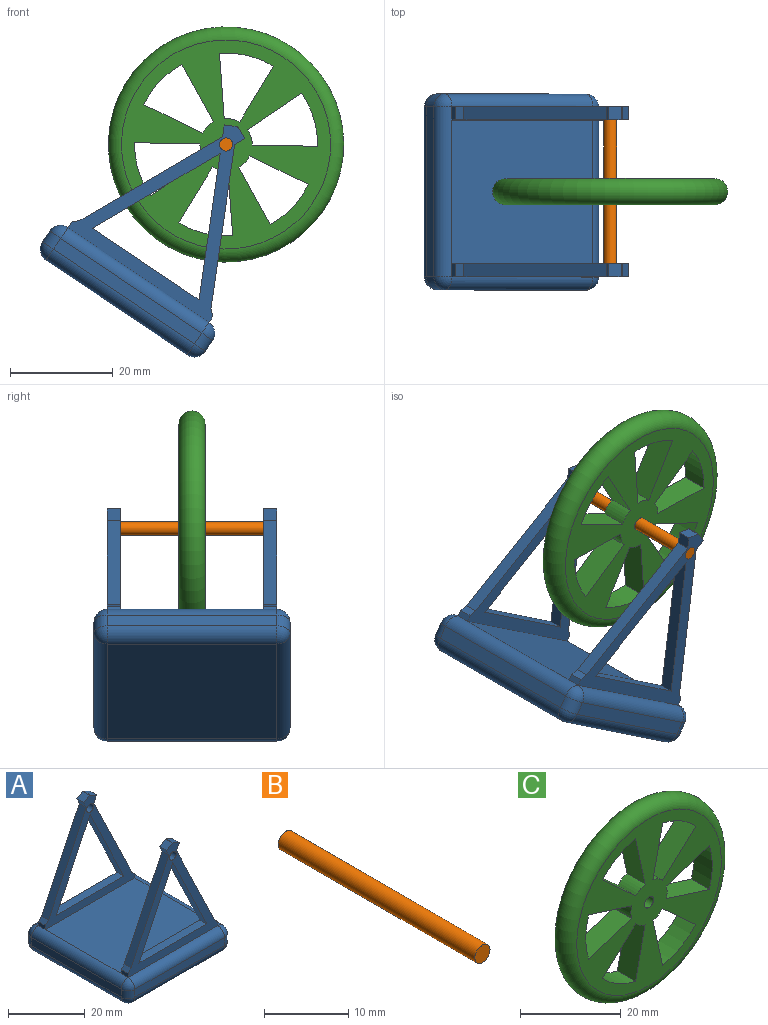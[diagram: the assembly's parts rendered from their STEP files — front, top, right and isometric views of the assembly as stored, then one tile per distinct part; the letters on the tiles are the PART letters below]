
ASSEMBLY  parts=3 mates=2
PART A: 60 faces, bbox 38.1x38.1x42.2 mm
  f0: plane 24.94x2.54mm, normal (0,0,1), area 63.3mm2, adj f1,f32,f34,f50
  f1: plane 25.94x12.47mm, normal (0.9,0,-0.43), area 73.1mm2, adj f0,f32,f34,f50
  f2: plane 28.96x13.92mm, normal (-0.9,0,0.43), area 81.6mm2, adj f32,f34,f49,f53
  f3: plane 24.94x2.54mm, normal (0,0,1), area 63.3mm2, adj f4,f37,f39,f46
  f4: plane 25.94x12.47mm, normal (0.9,0,-0.43), area 73.1mm2, adj f3,f37,f39,f46
  f5: plane 28.96x13.92mm, normal (-0.9,0,0.43), area 81.6mm2, adj f37,f39,f45,f52
  f6: plane 33.02x27.94mm, normal (0,0,1), area 922.6mm2, adj f16,f25,f32,f37
  f7: plane 33.02x2.54mm, normal (-1,0,0), area 83.9mm2, adj f20,f25,f28,f31
  f8: plane 33.02x2.54mm, normal (0,-1,0), area 83.9mm2, adj f17,f26,f27,f31
  f9: plane 33.02x2.54mm, normal (1,0,0), area 83.9mm2, adj f12,f16,f17,f18
  f10: plane 33.02x2.54mm, normal (0,1,0), area 83.9mm2, adj f12,f15,f19,f20
  f11: plane 33.02x33.02mm, normal (0,0,-1), area 1090.3mm2, adj f18,f19,f27,f28
  f12: cylinder r=2.54mm len=2.54mm, axis (0,0,1), area 10.1mm2, adj f9,f10,f13,f14
  f13: sphere r=2.54mm, area 10.1mm2, adj f12,f15,f16
  f14: sphere r=2.54mm, area 10.1mm2, adj f12,f18,f19
  f15: cylinder r=2.54mm len=33.02mm, axis (1,0,0), area 131.7mm2, adj f10,f13,f21,f34
  f16: cylinder r=2.54mm len=33.02mm, axis (0,-1,0), area 131.7mm2, adj f6,f9,f13,f22,f33,f36
  f17: cylinder r=2.54mm len=2.54mm, axis (0,0,-1), area 10.1mm2, adj f8,f9,f22,f23
  f18: cylinder r=2.54mm len=33.02mm, axis (0,1,0), area 131.7mm2, adj f9,f11,f14,f23
  f19: cylinder r=2.54mm len=33.02mm, axis (-1,0,0), area 131.7mm2, adj f10,f11,f14,f24
  f20: cylinder r=2.54mm len=2.54mm, axis (0,0,-1), area 10.1mm2, adj f7,f10,f21,f24
  f21: sphere r=2.54mm, area 10.1mm2, adj f15,f20,f25
  f22: sphere r=2.54mm, area 10.1mm2, adj f16,f17,f26
  f23: sphere r=2.54mm, area 10.1mm2, adj f17,f18,f27
  f24: sphere r=2.54mm, area 10.1mm2, adj f19,f20,f28
  f25: cylinder r=2.54mm len=33.02mm, axis (0,1,0), area 131.7mm2, adj f6,f7,f21,f29,f35,f38
  f26: cylinder r=2.54mm len=33.02mm, axis (-1,0,0), area 131.7mm2, adj f8,f22,f29,f39
  f27: cylinder r=2.54mm len=33.02mm, axis (1,0,0), area 131.7mm2, adj f8,f11,f23,f30
  f28: cylinder r=2.54mm len=33.02mm, axis (0,-1,0), area 131.7mm2, adj f7,f11,f24,f30
  f29: sphere r=2.54mm, area 10.1mm2, adj f25,f26,f31
  f30: sphere r=2.54mm, area 10.1mm2, adj f27,f28,f31
  f31: cylinder r=2.54mm len=2.54mm, axis (0,0,1), area 10.1mm2, adj f7,f8,f29,f30
  f32: plane 34.6x33.02mm, normal (0,-1,0), area 246.6mm2, adj f0,f1,f2,f6,f33,f35,f42,f43
  f33: plane 2.54x1.27mm, normal (1,0,0), area 3.2mm2, adj f16,f32,f34,f54
  f34: plane 34.6x33.02mm, normal (0,1,0), area 246.6mm2, adj f0,f1,f2,f15,f33,f35,f42,f43
  f35: plane 2.54x1.27mm, normal (-1,0,0), area 3.2mm2, adj f25,f32,f34,f53
  f36: plane 2.54x1.27mm, normal (1,0,0), area 3.2mm2, adj f16,f37,f39,f55
  f37: plane 34.6x33.02mm, normal (0,1,0), area 246.6mm2, adj f3,f4,f5,f6,f36,f38,f40,f41
  f38: plane 2.54x1.27mm, normal (-1,0,0), area 3.2mm2, adj f25,f37,f39,f52
  f39: plane 34.6x33.02mm, normal (0,-1,0), area 246.6mm2, adj f3,f4,f5,f26,f36,f38,f40,f41
  f40: plane 2.54x2.29mm, normal (0.43,0,0.9), area 6.5mm2, adj f37,f39,f41,f57
  f41: plane 2.54x2.09mm, normal (0.9,0,-0.43), area 5.9mm2, adj f37,f39,f40,f47
  f42: plane 2.54x2.29mm, normal (0.43,0,0.9), area 6.5mm2, adj f32,f34,f43,f56
  f43: plane 2.54x2.09mm, normal (0.9,0,-0.43), area 5.9mm2, adj f32,f34,f42,f51
  f44: plane 2.54x2.29mm, normal (-0.43,0,0.9), area 6.5mm2, adj f37,f39,f45,f57
  f45: plane 2.54x2.09mm, normal (-0.9,0,-0.43), area 5.9mm2, adj f5,f37,f39,f44
  f46: plane 25.94x12.47mm, normal (-0.9,0,-0.43), area 73.1mm2, adj f3,f4,f37,f39
  f47: plane 28.96x13.92mm, normal (0.9,0,0.43), area 81.6mm2, adj f37,f39,f41,f55
  f48: plane 2.54x2.29mm, normal (-0.43,0,0.9), area 6.5mm2, adj f32,f34,f49,f56
  f49: plane 2.54x2.09mm, normal (-0.9,0,-0.43), area 5.9mm2, adj f2,f32,f34,f48
  f50: plane 25.94x12.47mm, normal (-0.9,0,-0.43), area 73.1mm2, adj f0,f1,f32,f34
  f51: plane 28.96x13.92mm, normal (0.9,0,0.43), area 81.6mm2, adj f32,f34,f43,f54
  f52: plane 2.54x1.18mm, normal (-0.71,0,0.71), area 4.2mm2, adj f5,f37,f38,f39
  f53: plane 2.54x1.18mm, normal (-0.71,0,0.71), area 4.2mm2, adj f2,f32,f34,f35
  f54: plane 2.54x1.18mm, normal (0.71,0,0.71), area 4.2mm2, adj f32,f33,f34,f51
  f55: plane 2.54x1.18mm, normal (0.71,0,0.71), area 4.2mm2, adj f36,f37,f39,f47
  f56: cylinder r=5.08mm len=2.54mm, axis (0,1,0), area 0.6mm2, adj f32,f34,f42,f48
  f57: cylinder r=5.08mm len=2.54mm, axis (0,1,0), area 0.6mm2, adj f37,f39,f40,f44
  f58: cylinder r=1.27mm len=2.54mm, axis (0,-1,0), area 20.3mm2, adj f37,f39
  f59: cylinder r=1.27mm len=2.54mm, axis (0,-1,0), area 20.3mm2, adj f32,f34
PART B: 3 faces, bbox 2.5x33x2.5 mm
  f0: cylinder r=1.27mm len=33.02mm, axis (0,-1,0), area 263.5mm2, adj f1,f2
  f1: plane 2.54x2.54mm, normal (0,1,0), area 5.1mm2, adj f0
  f2: plane 2.54x2.54mm, normal (0,-1,0), area 5.1mm2, adj f0
PART C: 28 faces, bbox 49.5x5.1x49.5 mm
  f0: cylinder r=17.78mm len=9.33mm, axis (0,1,0), area 55.6mm2, adj f1,f19,f25,f26
  f1: plane 12.41x5.08mm, normal (-0.98,0,-0.21), area 64.5mm2, adj f0,f2,f25,f26
  f2: cylinder r=5.08mm len=5.08mm, axis (0,1,0), area 15.9mm2, adj f1,f19,f25,f26
  f3: cylinder r=17.78mm len=9.33mm, axis (0,1,0), area 55.6mm2, adj f4,f20,f25,f26
  f4: plane 9.38x8.56mm, normal (-0.67,0,0.74), area 64.5mm2, adj f3,f5,f25,f26
  f5: cylinder r=5.08mm len=5.08mm, axis (0,1,0), area 15.9mm2, adj f4,f20,f25,f26
  f6: cylinder r=17.78mm len=10.77mm, axis (0,1,0), area 55.6mm2, adj f7,f21,f25,f26
  f7: plane 12.1x5.08mm, normal (0.3,0,0.95), area 64.5mm2, adj f6,f8,f25,f26
  f8: cylinder r=5.08mm len=5.08mm, axis (0,1,0), area 15.9mm2, adj f7,f21,f25,f26
  f9: cylinder r=17.78mm len=9.33mm, axis (0,1,0), area 55.6mm2, adj f10,f22,f25,f26
  f10: plane 12.41x5.08mm, normal (0.98,0,0.21), area 64.5mm2, adj f9,f11,f25,f26
  f11: cylinder r=5.08mm len=5.08mm, axis (0,1,0), area 15.9mm2, adj f10,f22,f25,f26
  f12: cylinder r=17.78mm len=9.33mm, axis (0,1,0), area 55.6mm2, adj f13,f23,f25,f26
  f13: plane 9.38x8.56mm, normal (0.67,0,-0.74), area 64.5mm2, adj f12,f14,f25,f26
  f14: cylinder r=5.08mm len=5.08mm, axis (0,1,0), area 15.9mm2, adj f13,f23,f25,f26
  f15: cylinder r=17.78mm len=10.77mm, axis (0,1,0), area 55.6mm2, adj f16,f24,f25,f26
  f16: plane 12.1x5.08mm, normal (-0.3,0,-0.95), area 64.5mm2, adj f15,f17,f25,f26
  f17: cylinder r=5.08mm len=5.08mm, axis (0,1,0), area 15.9mm2, adj f16,f24,f25,f26
  f18: cylinder r=1.27mm len=5.08mm, axis (0,1,0), area 40.5mm2, adj f25,f26
  f19: plane 9.38x8.56mm, normal (0.67,0,0.74), area 64.5mm2, adj f0,f2,f25,f26
  f20: plane 12.41x5.08mm, normal (0.98,0,-0.21), area 64.5mm2, adj f3,f5,f25,f26
  f21: plane 12.1x5.08mm, normal (0.3,0,-0.95), area 64.5mm2, adj f6,f8,f25,f26
  f22: plane 9.38x8.56mm, normal (-0.67,0,-0.74), area 64.5mm2, adj f9,f11,f25,f26
  f23: plane 12.41x5.08mm, normal (-0.98,0,0.21), area 64.5mm2, adj f12,f14,f25,f26
  f24: plane 12.1x5.08mm, normal (-0.3,0,0.95), area 64.5mm2, adj f15,f17,f25,f26
  f25: plane 40.64x40.64mm, normal (0,-1,0), area 756.2mm2, adj f0,f1,f2,f3,f4,f5,f6,f7
  f26: plane 40.64x40.64mm, normal (0,1,0), area 756.2mm2, adj f0,f1,f2,f3,f4,f5,f6,f7
  f27: torus R=20.32mm, axis (0,-1,0), area 1099.9mm2, adj f25,f26
PLACE A rot(axis=(0,1,0),33.9deg) t=(-57.31,0,29.73)mm fixed
PLACE B rot(axis=(0,1,0),33.9deg) t=(-57.31,0,29.73)mm
PLACE C rot(axis=(0,-1,0),76.5deg) t=(1.06,0,52.49)mm
MATE fastened B.f0 <-> A.f58  axis (0,-1,0) through (-36.04,-16.51,61.39)mm
MATE revolute B.f0 <-> C.f9  axis (0,-1,0) through (-36.04,0,61.39)mm
